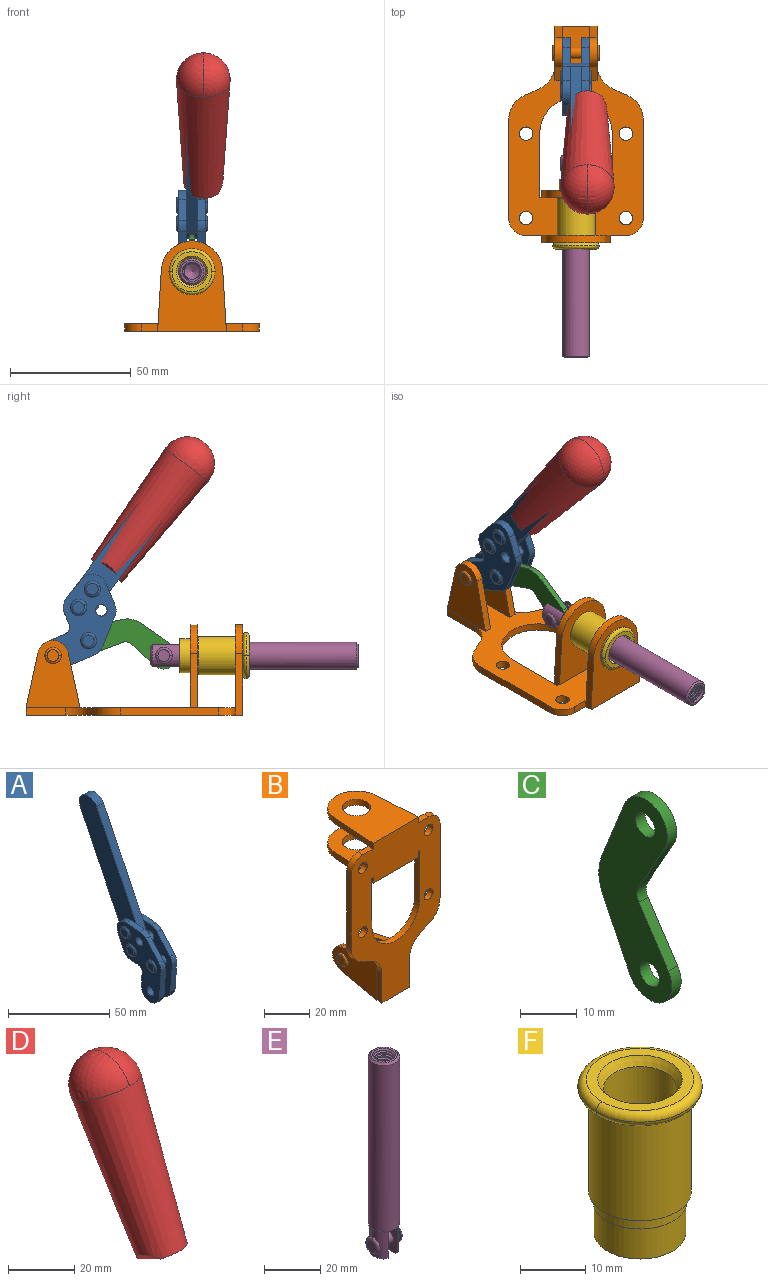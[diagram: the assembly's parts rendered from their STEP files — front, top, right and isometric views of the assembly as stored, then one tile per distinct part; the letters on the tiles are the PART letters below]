
ASSEMBLY  parts=6 mates=6
PART A: 59 faces, bbox 12.9x60.2x99.6 mm
  f0: torus R=2.39mm, axis (-1,0,0), area 14.9mm2, adj f20,f43,f51
  f1: torus R=2.39mm, axis (-1,0,0), area 14.9mm2, adj f19,f42,f51
  f2: torus R=2.39mm, axis (-1,0,0), area 14.9mm2, adj f18,f35,f51
  f3: torus R=2.39mm, axis (-1,0,0), area 14.9mm2, adj f14,f17,f23
  f4: torus R=2.39mm, axis (-1,0,0), area 14.9mm2, adj f13,f16,f23
  f5: torus R=2.39mm, axis (-1,0,0), area 14.9mm2, adj f12,f15,f23
  f6: cylinder r=2.39mm len=4.78mm, axis (1,0,0), area 46.5mm2, adj f48,f50,f51
  f7: cylinder r=2.39mm len=4.78mm, axis (1,0,0), area 46.5mm2, adj f50,f51
  f8: cylinder r=6.35mm len=12.68mm, axis (1,0,0), area 61.8mm2, adj f38,f39,f50,f51
  f9: cylinder r=2.39mm len=4.78mm, axis (-1,0,0), area 70.5mm2, adj f46,f50
  f10: cylinder r=2.39mm len=4.78mm, axis (-1,0,0), area 46.5mm2, adj f23,f45,f46
  f11: cylinder r=2.39mm len=4.78mm, axis (-1,0,0), area 46.5mm2, adj f23,f46
  f12: plane 4.78x4.78mm, normal (1,0,0), area 17.9mm2, adj f5,f15
  f13: plane 4.78x4.78mm, normal (1,0,0), area 17.9mm2, adj f4,f16
  f14: plane 4.78x4.78mm, normal (1,0,0), area 17.9mm2, adj f3,f17
  f15: torus R=2.39mm, axis (-1,0,0), area 14.9mm2, adj f5,f12,f23
  f16: torus R=2.39mm, axis (-1,0,0), area 14.9mm2, adj f4,f13,f23
  f17: torus R=2.39mm, axis (-1,0,0), area 14.9mm2, adj f3,f14,f23
  f18: plane 4.78x4.78mm, normal (-1,0,0), area 17.9mm2, adj f2,f35
  f19: plane 4.78x4.78mm, normal (-1,0,0), area 17.9mm2, adj f1,f42
  f20: plane 4.78x4.78mm, normal (-1,0,0), area 17.9mm2, adj f0,f43
  f21: plane 2.26x0.2mm, normal (1,0,0), area 0.2mm2, adj f31,f44
  f22: plane 2.26x0.2mm, normal (-1,0,0), area 0.2mm2, adj f41,f44
  f23: plane 39.37x30.77mm, normal (1,0,0), area 565.5mm2, adj f3,f4,f5,f10,f11,f15,f16,f17
  f24: cylinder r=6.1mm len=4.15mm, axis (-1,0,0), area 14.7mm2, adj f23,f25,f32,f46
  f25: plane 10.25x9.01mm, normal (0,-0.75,0.66), area 42.3mm2, adj f23,f24,f26,f46
  f26: cylinder r=6.35mm len=4.64mm, axis (-1,0,0), area 15.6mm2, adj f23,f25,f27,f46
  f27: plane 15.84x3.1mm, normal (0,-1,-0.07), area 49.2mm2, adj f23,f26,f28,f46
  f28: cylinder r=6.35mm len=12.68mm, axis (-1,0,0), area 61.8mm2, adj f23,f27,f29,f46
  f29: plane 8.11x3.1mm, normal (0,1,0.07), area 25.2mm2, adj f23,f28,f30,f46
  f30: cylinder r=3.05mm len=3.25mm, axis (-1,0,0), area 14.8mm2, adj f23,f29,f31,f46
  f31: plane 5.99x3.1mm, normal (0,0.07,-1), area 18.6mm2, adj f21,f23,f30,f44,f46
  f32: plane 9.5x3.1mm, normal (0,-0.07,1), area 29.5mm2, adj f23,f24,f33,f46,f47
  f33: cylinder r=6.1mm len=8.63mm, axis (-1,0,0), area 39.1mm2, adj f23,f32,f34,f47
  f34: plane 8.65x3.96mm, normal (0,0.91,-0.42), area 29.5mm2, adj f23,f33,f44,f47
  f35: torus R=2.39mm, axis (-1,0,0), area 14.9mm2, adj f2,f18,f51
  f36: plane 10.25x9.01mm, normal (0,-0.75,0.66), area 42.3mm2, adj f37,f49,f50,f51
  f37: cylinder r=6.35mm len=4.64mm, axis (1,0,0), area 15.6mm2, adj f36,f38,f50,f51
  f38: plane 15.84x3.1mm, normal (0,-1,-0.07), area 49.2mm2, adj f8,f37,f50,f51
  f39: plane 8.11x3.1mm, normal (0,1,0.07), area 25.2mm2, adj f8,f40,f50,f51
  f40: cylinder r=3.05mm len=3.25mm, axis (1,0,0), area 14.8mm2, adj f39,f41,f50,f51
  f41: plane 5.99x3.1mm, normal (0,0.07,-1), area 18.6mm2, adj f22,f40,f44,f50,f51
  f42: torus R=2.39mm, axis (-1,0,0), area 14.9mm2, adj f1,f19,f51
  f43: torus R=2.39mm, axis (-1,0,0), area 14.9mm2, adj f0,f20,f51
  f44: cylinder r=6.35mm len=12.12mm, axis (-1,0,0), area 128.9mm2, adj f21,f22,f23,f31,f34,f41,f46,f47
  f45: plane 2.65x1.35mm, normal (1,0,0), area 1mm2, adj f10,f55
  f46: plane 39.08x20.42mm, normal (-1,0,0), area 412.5mm2, adj f9,f10,f11,f24,f25,f26,f27,f28
  f47: plane 77.62x39.82mm, normal (1,0,0), area 850mm2, adj f32,f33,f34,f44,f53,f54,f55
  f48: plane 2.65x1.35mm, normal (-1,0,0), area 1mm2, adj f6,f55
  f49: cylinder r=6.1mm len=4.15mm, axis (1,0,0), area 14.7mm2, adj f36,f50,f51,f56
  f50: plane 39.08x20.42mm, normal (1,0,0), area 412.5mm2, adj f6,f7,f8,f9,f36,f37,f38,f39
  f51: plane 39.37x30.77mm, normal (-1,0,0), area 565.5mm2, adj f0,f1,f2,f6,f7,f8,f35,f36
  f52: plane 8.65x3.96mm, normal (0,0.91,-0.42), area 29.5mm2, adj f44,f51,f57,f58
  f53: plane 68.49x33.4mm, normal (0,0.9,-0.44), area 358.1mm2, adj f44,f47,f54,f58
  f54: cylinder r=6.35mm len=12.06mm, axis (1,0,0), area 93.7mm2, adj f47,f53,f55,f58
  f55: plane 68.49x33.4mm, normal (0,-0.9,0.44), area 358.1mm2, adj f44,f45,f46,f47,f48,f50,f54,f58
  f56: plane 9.5x3.1mm, normal (0,-0.07,1), area 29.5mm2, adj f49,f50,f51,f57,f58
  f57: cylinder r=6.1mm len=8.63mm, axis (1,0,0), area 39.1mm2, adj f51,f52,f56,f58
  f58: plane 77.62x39.82mm, normal (-1,0,0), area 850mm2, adj f44,f52,f53,f54,f55,f56,f57
PART B: 55 faces, bbox 55.7x37.4x89.8 mm
  f0: torus R=2.41mm, axis (-1,0,0), area 15mm2, adj f11,f15,f25
  f1: torus R=2.41mm, axis (-1,0,0), area 15mm2, adj f10,f12,f22
  f2: cylinder r=2.78mm len=5.56mm, axis (0,-1,0), area 54.2mm2, adj f30,f54
  f3: cylinder r=14.99mm len=29.97mm, axis (0,-1,0), area 145.9mm2, adj f30,f49,f53,f54
  f4: cylinder r=2.78mm len=5.56mm, axis (0,-1,0), area 54.2mm2, adj f30,f54
  f5: cylinder r=2.78mm len=5.56mm, axis (0,-1,0), area 54.2mm2, adj f30,f54
  f6: cylinder r=2.78mm len=5.56mm, axis (0,-1,0), area 54.2mm2, adj f30,f54
  f7: cylinder r=6.35mm len=12.7mm, axis (0,0,1), area 123.6mm2, adj f27,f51
  f8: cylinder r=6.35mm len=12.7mm, axis (0,0,-1), area 124.7mm2, adj f21,f35
  f9: cylinder r=2.41mm len=11.18mm, axis (-1,0,0), area 169.4mm2, adj f16,f19
  f10: plane 4.83x4.83mm, normal (1,0,0), area 18.3mm2, adj f1,f12
  f11: plane 4.83x4.83mm, normal (-1,0,0), area 18.3mm2, adj f0,f15
  f12: torus R=2.41mm, axis (-1,0,0), area 15mm2, adj f1,f10,f22
  f13: cylinder r=6.35mm len=12.41mm, axis (1,0,0), area 53.4mm2, adj f18,f19,f22,f23
  f14: cylinder r=6.35mm len=12.41mm, axis (-1,0,0), area 53.4mm2, adj f16,f17,f24,f25
  f15: torus R=2.41mm, axis (-1,0,0), area 15mm2, adj f0,f11,f25
  f16: plane 27.86x22.35mm, normal (1,0,0), area 425.4mm2, adj f9,f14,f17,f24,f30
  f17: plane 22.86x4.97mm, normal (0,0.21,0.98), area 72.5mm2, adj f14,f16,f25,f30
  f18: plane 22.86x4.97mm, normal (0,0.21,0.98), area 72.5mm2, adj f13,f19,f22,f30
  f19: plane 27.86x22.35mm, normal (-1,0,0), area 425.4mm2, adj f9,f13,f18,f23,f30
  f20: cylinder r=12.7mm len=25.35mm, axis (0,0,-1), area 119.8mm2, adj f21,f34,f35,f36
  f21: plane 34.21x28.07mm, normal (0,0,-1), area 702.4mm2, adj f8,f20,f30,f34,f36
  f22: plane 27.96x22.45mm, normal (1,0,0), area 407.2mm2, adj f1,f12,f13,f18,f23,f30,f42,f43
  f23: plane 22.86x4.97mm, normal (0,0.21,-0.98), area 72.5mm2, adj f13,f19,f22,f44
  f24: plane 22.86x4.97mm, normal (0,0.21,-0.98), area 72.5mm2, adj f14,f16,f25,f44
  f25: plane 27.86x22.35mm, normal (-1,0,0), area 407.1mm2, adj f0,f14,f15,f17,f24,f30,f45,f46
  f26: plane 3.1x0.95mm, normal (0,0,-1), area 2.7mm2, adj f30,f49,f50,f54
  f27: plane 34.21x28.07mm, normal (0,0,1), area 702.4mm2, adj f7,f28,f30,f50,f52
  f28: cylinder r=12.7mm len=25.35mm, axis (0,0,1), area 118.8mm2, adj f27,f50,f51,f52
  f29: plane 3.1x0.95mm, normal (0,0,-1), area 2.7mm2, adj f30,f52,f53,f54
  f30: plane 86.54x55.63mm, normal (0,1,0), area 2362.9mm2, adj f2,f3,f4,f5,f6,f16,f17,f18
  f31: plane 40.56x3.1mm, normal (-1,0,0), area 125.7mm2, adj f30,f32,f48,f54
  f32: cylinder r=7.11mm len=7.11mm, axis (0,-1,0), area 34.6mm2, adj f30,f31,f33,f54
  f33: plane 6.67x3.1mm, normal (0,0,1), area 20.4mm2, adj f30,f32,f34,f54
  f34: plane 25.39x3.13mm, normal (-1,0.06,0), area 79.5mm2, adj f20,f21,f33,f35,f54
  f35: plane 37.31x28.45mm, normal (0,0,1), area 789.9mm2, adj f8,f20,f34,f36,f54
  f36: plane 25.39x3.13mm, normal (1,0.06,0), area 79.5mm2, adj f20,f21,f35,f37,f54
  f37: plane 6.67x3.1mm, normal (0,0,1), area 20.4mm2, adj f30,f36,f38,f54
  f38: cylinder r=7.11mm len=7.11mm, axis (0,-1,0), area 34.6mm2, adj f30,f37,f39,f54
  f39: plane 40.56x3.1mm, normal (1,0,0), area 125.7mm2, adj f30,f38,f40,f54
  f40: cylinder r=11.18mm len=10.16mm, axis (0,-1,0), area 39.5mm2, adj f30,f39,f41,f54
  f41: plane 6.09x3.1mm, normal (0.42,0,-0.91), area 20.8mm2, adj f30,f40,f42,f54
  f42: cylinder r=11.18mm len=9.41mm, axis (0,-1,0), area 37.2mm2, adj f22,f30,f41,f43,f54
  f43: plane 16.5x3.1mm, normal (1,0,0), area 51.1mm2, adj f22,f42,f44,f54
  f44: plane 17.37x3.1mm, normal (0,0,-1), area 53.8mm2, adj f23,f24,f30,f43,f45,f54
  f45: plane 16.5x3.1mm, normal (-1,0,0), area 51.1mm2, adj f25,f44,f46,f54
  f46: cylinder r=11.18mm len=9.41mm, axis (0,-1,0), area 37.2mm2, adj f25,f30,f45,f47,f54
  f47: plane 6.09x3.1mm, normal (-0.42,0,-0.91), area 20.8mm2, adj f30,f46,f48,f54
  f48: cylinder r=11.18mm len=10.16mm, axis (0,-1,0), area 39.5mm2, adj f30,f31,f47,f54
  f49: plane 26.54x3.1mm, normal (-1,0,0), area 82.3mm2, adj f3,f26,f30,f54
  f50: plane 25.39x3.1mm, normal (1,0.06,0), area 78.8mm2, adj f26,f27,f28,f51,f54
  f51: plane 37.31x28.45mm, normal (0,0,-1), area 789.9mm2, adj f7,f28,f50,f52,f54
  f52: plane 25.39x3.1mm, normal (-1,0.06,0), area 78.8mm2, adj f27,f28,f29,f51,f54
  f53: plane 26.54x3.1mm, normal (1,0,0), area 82.3mm2, adj f3,f29,f30,f54
  f54: plane 89.66x55.63mm, normal (0,-1,0), area 2678.5mm2, adj f2,f3,f4,f5,f6,f26,f29,f31
PART C: 12 faces, bbox 2.3x18.2x42.8 mm
  f0: cylinder r=2.4mm len=4.8mm, axis (1,0,0), area 34.9mm2, adj f4,f11
  f1: cylinder r=10.41mm len=8.47mm, axis (1,0,0), area 20.2mm2, adj f4,f9,f10,f11
  f2: cylinder r=3.05mm len=3.16mm, axis (1,0,0), area 7.7mm2, adj f4,f6,f7,f11
  f3: cylinder r=2.4mm len=4.8mm, axis (1,0,0), area 34.9mm2, adj f4,f11
  f4: plane 42.81x18.23mm, normal (-1,0,0), area 414.1mm2, adj f0,f1,f2,f3,f5,f6,f7,f8
  f5: cylinder r=5.54mm len=10.67mm, axis (1,0,0), area 41.8mm2, adj f4,f6,f10,f11
  f6: plane 11.66x6.53mm, normal (0,-0.87,-0.49), area 30.9mm2, adj f2,f4,f5,f11
  f7: plane 11.17x7.33mm, normal (0,-0.84,0.55), area 30.9mm2, adj f2,f4,f8,f11
  f8: cylinder r=5.54mm len=10.51mm, axis (1,0,0), area 41.8mm2, adj f4,f7,f9,f11
  f9: plane 13.67x6.67mm, normal (0,0.9,-0.44), area 35.1mm2, adj f1,f4,f8,f11
  f10: plane 14.1x5.7mm, normal (0,0.93,0.37), area 35.1mm2, adj f1,f4,f5,f11
  f11: plane 42.81x18.23mm, normal (1,0,0), area 414.1mm2, adj f0,f1,f2,f3,f5,f6,f7,f8
PART D: 11 faces, bbox 22.3x42.6x64.5 mm
  f0: sphere r=11.13mm, area 411.4mm2, adj f1,f8
  f1: cone r=11.11mm half-angle=3.3deg, axis (0,0.44,0.9), area 3251.8mm2, adj f0,f7,f8,f9,f10
  f2: cylinder r=6.16mm len=11.7mm, axis (1,0,0), area 89.5mm2, adj f3,f4,f5,f6
  f3: plane 60.23x36.75mm, normal (-1,0,0), area 763.6mm2, adj f2,f4,f6,f10
  f4: plane 51.37x25.05mm, normal (0,0.9,-0.44), area 264.2mm2, adj f2,f3,f5,f10
  f5: plane 60.23x36.75mm, normal (1,0,0), area 763.6mm2, adj f2,f4,f6,f10
  f6: plane 51.37x25.05mm, normal (0,-0.9,0.44), area 264.2mm2, adj f2,f3,f5,f10
  f7: plane 9.95x5.95mm, normal (0.71,-0.31,-0.64), area 25.8mm2, adj f1,f10
  f8: sphere r=11.13mm, area 411.4mm2, adj f0,f1
  f9: plane 9.95x5.95mm, normal (-0.71,-0.31,-0.64), area 25.8mm2, adj f1,f10
  f10: plane 14.27x11.38mm, normal (0,-0.44,-0.9), area 106.7mm2, adj f1,f3,f4,f5,f6,f7,f9
PART E: 48 faces, bbox 12.6x11.1x86.1 mm
  f0: torus R=2.41mm, axis (-1,0,0), area 15mm2, adj f30,f32,f34
  f1: torus R=2.41mm, axis (-1,0,0), area 15mm2, adj f29,f31,f33
  f2: cylinder r=5.54mm len=72.39mm, axis (0,0,1), area 2518.5mm2, adj f3,f4,f42,f43
  f3: cone r=5.54mm half-angle=45deg, axis (0,0,1), area 7.6mm2, adj f2,f5,f41
  f4: cone r=5.54mm half-angle=45deg, axis (0,0,-1), area 34.9mm2, adj f2,f39
  f5: cylinder r=5.08mm len=11.48mm, axis (0,0,1), area 108.3mm2, adj f3,f7,f8,f41
  f6: cylinder r=2.41mm len=4.83mm, axis (-1,0,0), area 71.2mm2, adj f40,f41
  f7: cylinder r=2.41mm len=4.83mm, axis (-1,0,0), area 7.6mm2, adj f5,f34
  f8: cone r=5.08mm half-angle=45deg, axis (0,0,1), area 10.6mm2, adj f5,f37,f41
  f9: cone r=3.98mm half-angle=45deg, axis (0,0,1), area 17.6mm2, adj f27,f39,f45,f46,f47
  f10: cylinder r=2.41mm len=4.83mm, axis (-1,0,0), area 7.6mm2, adj f33,f38
  f11: cylinder r=3.2mm len=6.4mm, axis (0,0,1), area 78.4mm2, adj f12,f28,f44,f45,f47
  f12: cylinder r=3.2mm len=6.4mm, axis (0,0,1), area 10.5mm2, adj f11,f13,f45,f47
  f13: cylinder r=3.2mm len=6.4mm, axis (0,0,1), area 10.5mm2, adj f12,f14,f45,f47
  f14: cylinder r=3.2mm len=6.4mm, axis (0,0,1), area 10.5mm2, adj f13,f15,f45,f47
  f15: cylinder r=3.2mm len=6.4mm, axis (0,0,1), area 10.5mm2, adj f14,f16,f45,f47
  f16: cylinder r=3.2mm len=6.4mm, axis (0,0,1), area 10.5mm2, adj f15,f17,f45,f47
  f17: cylinder r=3.2mm len=6.4mm, axis (0,0,1), area 10.5mm2, adj f16,f18,f45,f47
  f18: cylinder r=3.2mm len=6.4mm, axis (0,0,1), area 10.5mm2, adj f17,f19,f45,f47
  f19: cylinder r=3.2mm len=6.4mm, axis (0,0,1), area 10.5mm2, adj f18,f20,f45,f47
  f20: cylinder r=3.2mm len=6.4mm, axis (0,0,1), area 10.5mm2, adj f19,f21,f45,f47
  f21: cylinder r=3.2mm len=6.4mm, axis (0,0,1), area 10.5mm2, adj f20,f22,f45,f47
  f22: cylinder r=3.2mm len=6.4mm, axis (0,0,1), area 10.5mm2, adj f21,f23,f45,f47
  f23: cylinder r=3.2mm len=6.4mm, axis (0,0,1), area 10.5mm2, adj f22,f24,f45,f47
  f24: cylinder r=3.2mm len=6.4mm, axis (0,0,1), area 10.5mm2, adj f23,f25,f45,f47
  f25: cylinder r=3.2mm len=6.4mm, axis (0,0,1), area 10.5mm2, adj f24,f26,f45,f47
  f26: cylinder r=3.2mm len=6.4mm, axis (0,0,1), area 10.5mm2, adj f25,f27,f45,f47
  f27: cylinder r=3.2mm len=6.4mm, axis (0,0,1), area 7.4mm2, adj f9,f26,f45,f47
  f28: cone r=3.2mm half-angle=60deg, axis (0,0,1), area 37.2mm2, adj f11
  f29: plane 4.83x4.83mm, normal (-1,0,0), area 18.3mm2, adj f1,f31
  f30: plane 4.83x4.83mm, normal (1,0,0), area 18.3mm2, adj f0,f32
  f31: torus R=2.41mm, axis (-1,0,0), area 15mm2, adj f1,f29,f33
  f32: torus R=2.41mm, axis (-1,0,0), area 15mm2, adj f0,f30,f34
  f33: plane 6.83x6.83mm, normal (1,0,0), area 18.3mm2, adj f1,f10,f31
  f34: plane 6.83x6.83mm, normal (-1,0,0), area 18.3mm2, adj f0,f7,f32
  f35: cone r=5.08mm half-angle=45deg, axis (0,0,1), area 10.6mm2, adj f36,f38,f40
  f36: plane 7.25x1.97mm, normal (0,0,-1), area 10mm2, adj f35,f40
  f37: plane 7.25x1.97mm, normal (0,0,-1), area 10mm2, adj f8,f41
  f38: cylinder r=5.08mm len=11.48mm, axis (0,0,1), area 108.3mm2, adj f10,f35,f40,f42
  f39: plane 9.55x9.55mm, normal (0,0,1), area 22mm2, adj f4,f9
  f40: plane 12.76x10.09mm, normal (1,0,0), area 95.7mm2, adj f6,f35,f36,f38,f42,f43
  f41: plane 12.76x10.09mm, normal (-1,0,0), area 95.7mm2, adj f3,f5,f6,f8,f37,f43
  f42: cone r=5.54mm half-angle=45deg, axis (0,0,1), area 7.6mm2, adj f2,f38,f40
  f43: plane 11.07x4.7mm, normal (0,0,-1), area 50.4mm2, adj f2,f40,f41
  f44: plane 0.89x0.62mm, normal (-1,0,0), area 0.3mm2, adj f11,f45,f46,f47
  f45: bspline ~24.8x7.63mm, area 266.6mm2, adj f9,f11,f12,f13,f14,f15,f16,f17
  f46: bspline ~24.87x7.63mm, area 73.6mm2, adj f9,f44,f45,f47
  f47: bspline ~24.98x7.63mm, area 272.5mm2, adj f9,f11,f12,f13,f14,f15,f16,f17
PART F: 15 faces, bbox 20.6x20.6x28.7 mm
  f0: torus R=8.26mm, axis (0,0,1), area 56.8mm2, adj f1,f10,f12
  f1: torus R=8.26mm, axis (0,0,1), area 56.8mm2, adj f0,f6,f13
  f2: cylinder r=5.59mm len=25.91mm, axis (0,0,1), area 909.6mm2, adj f3,f4
  f3: cone r=6.86mm half-angle=45deg, axis (0,0,-1), area 70.2mm2, adj f2,f14
  f4: cone r=6.47mm half-angle=30deg, axis (0,0,1), area 66.7mm2, adj f2,f13
  f5: cylinder r=7.04mm len=14.07mm, axis (0,0,1), area 252.6mm2, adj f11,f14
  f6: torus R=8.26mm, axis (0,0,1), area 56.8mm2, adj f1,f12,f13
  f7: cylinder r=7.16mm len=14.33mm, axis (0,0,1), area 91.5mm2, adj f9,f11
  f8: cylinder r=7.86mm len=18.42mm, axis (0,0,1), area 909.6mm2, adj f9,f10
  f9: plane 15.72x15.72mm, normal (0,0,-1), area 33mm2, adj f7,f8
  f10: plane 16.51x16.51mm, normal (0,0,-1), area 19.9mm2, adj f0,f8,f12
  f11: plane 14.33x14.33mm, normal (0,0,-1), area 5.7mm2, adj f5,f7
  f12: torus R=8.26mm, axis (0,0,1), area 56.8mm2, adj f0,f6,f10
  f13: plane 16.51x16.51mm, normal (0,0,1), area 82.7mm2, adj f1,f4,f6
  f14: plane 14.07x14.07mm, normal (0,0,-1), area 7.8mm2, adj f3,f5
PLACE A rot(axis=(1,0,0),63.2deg) t=(0,1.78,17.12)mm
PLACE B rot(axis=(1,0,0),90deg) t=(0,9.43,0)mm fixed
PLACE C rot(axis=(1,0,0),103.2deg) t=(0,16.42,4.18)mm
PLACE D rot(axis=(1,0,0),63.2deg) t=(4.66,1.78,17.12)mm
PLACE E rot(axis=(1,0,0),90deg) t=(0,11.22,0)mm
PLACE F rot(axis=(1,0,0),90deg) t=(0,9.43,0)mm
MATE revolute C.f5 <-> E.f6  axis (1,0,0) through (0,-4.26,24.61)mm
MATE slider E.f2 <-> B.f7  axis (0,-1,0) through (0,-47.56,24.61)mm
MATE revolute C.f3 <-> A.f4  axis (1,0,0) through (0,26.89,30.77)mm
MATE fastened F.f2 <-> B.f7  axis (0,1,0) through (0,-36.96,24.61)mm
MATE fastened D.f2 <-> A.f54  axis (1,0,0) through (2.35,-15.06,105.23)mm
MATE revolute B.f0 <-> A.f7  axis (-1,0,0) through (0,41.52,24.61)mm
